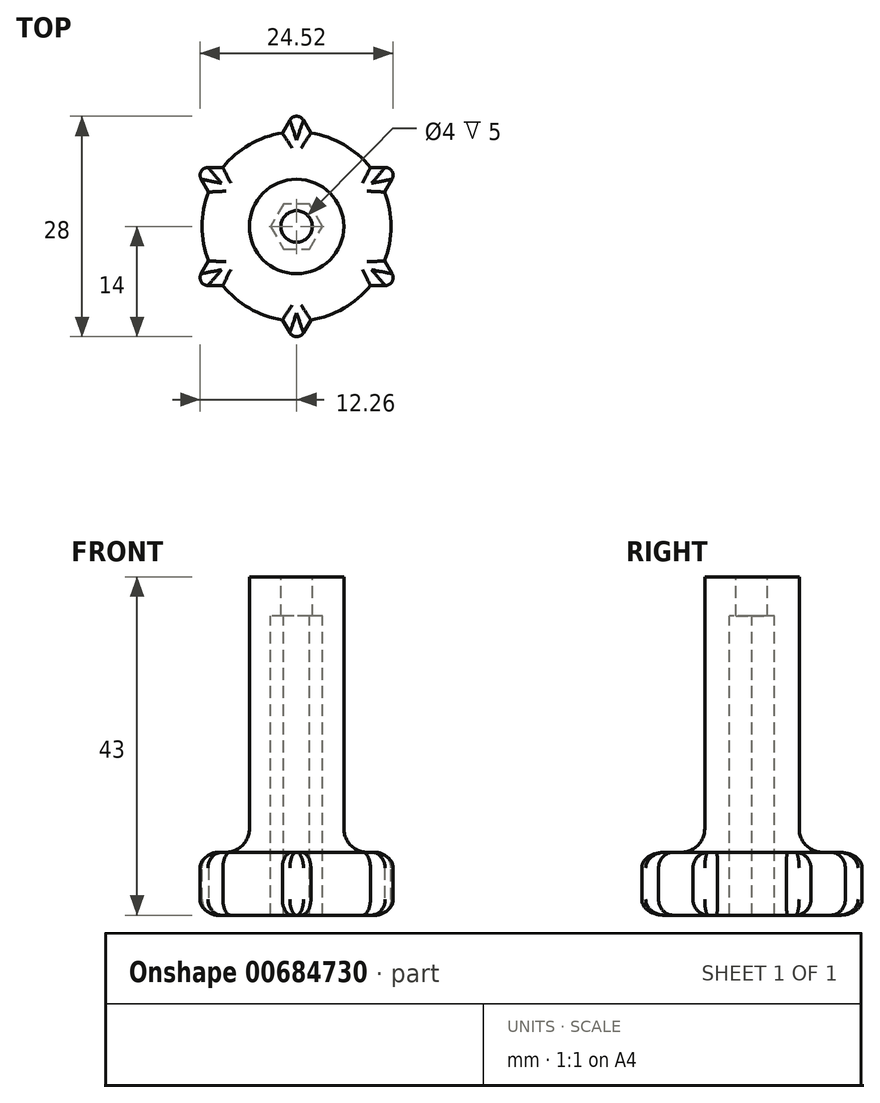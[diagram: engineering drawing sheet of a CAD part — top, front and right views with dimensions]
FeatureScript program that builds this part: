
annotation { "Feature Type Name" : "Feature", "Feature Type Description" : "" }
export const myFeature = defineFeature(function(context is Context, id is Id, definition is map)
    precondition{}
    {
        {
            var Q0;
            Q0=qCreatedBy(makeId("Front.planeOp"),FACE);
            var sketch = newSketch(context, id + "F0", { "sketchPlane" : qUnion([Q0])});
            skLineSegment(sketch, "E0", {"start": v(0, 0) * mm, "end": v(12, 0) * mm});
            skLineSegment(sketch, "E1", {"start": v(12, 0) * mm, "end": v(12, 8) * mm});
            skLineSegment(sketch, "E2", {"start": v(12, 8) * mm, "end": v(6, 8) * mm});
            skLineSegment(sketch, "E3", {"start": v(6, 8) * mm, "end": v(6, 43) * mm});
            skLineSegment(sketch, "E4", {"start": v(6, 43) * mm, "end": v(0, 43) * mm});
            skLineSegment(sketch, "E5", {"start": v(0, 43) * mm, "end": v(0, 0) * mm});
            skSolve(sketch);
        }
        {
            var Q0;
            Q0=makeQuery(id+"F0.imprint","IMPRINT",FACE,{"disambiguationData":[TD([[makeQuery(id+"F0.imprint","IMPRINT",EDGE,{"derivedFrom":sQuery(id+"F0.wireOp",EDGE,"E0")}),1.0]])]});
            var Q1;
            Q1=sQuery(id+"F0.wireOp",EDGE,"E5");
            revolve(context, id + "F1", {"surfaceOperationType" : NewSurfaceOperationType.NEW, "entities" : qUnion([Q0]), "axis" : qUnion([Q1]), "revolveType" : RevolveType.FULL});
        }
        {
            var Q0;
            Q0=makeQuery(id+"F1.opRevolve","SWEPT_EDGE",EDGE,{"disambiguationData":[OSD([sQuery(id+"F0.wireOp",EDGE,"E2"),sQuery(id+"F0.wireOp",EDGE,"E3")])]});
            fillet(context, id + "F2", {"entities" : qUnion([Q0]), "radius" : 3 * mm, "tangentPropagation" : true, "allowEdgeOverflow" : false});
        }
        {
            var Q0;
            Q0=makeQuery(id+"F1.opRevolve","SWEPT_FACE",FACE,{"disambiguationData":[OSD([sQuery(id+"F0.wireOp",EDGE,"E4")])]});
            var sketch = newSketch(context, id + "F3", { "sketchPlane" : qUnion([Q0])});
            skCircle(sketch, "E6", {"center": v(0, 0) * mm, "radius": 2 * mm});
            skCircle(sketch, "E7.cCircle", {"center": v(0, 0) * mm, "radius": 2.85 * mm, "construction": true});
            skLineSegment(sketch, "E7.0", {"start": v(1.65, 2.85) * mm, "end": v(3.3, 0) * mm});
            skLineSegment(sketch, "E7.1", {"start": v(3.3, 0) * mm, "end": v(1.65, -2.85) * mm});
            skLineSegment(sketch, "E7.2", {"start": v(1.65, -2.85) * mm, "end": v(-1.65, -2.85) * mm});
            skLineSegment(sketch, "E7.3", {"start": v(-1.65, -2.85) * mm, "end": v(-3.3, 0) * mm});
            skLineSegment(sketch, "E7.4", {"start": v(-3.3, 0) * mm, "end": v(-1.65, 2.85) * mm});
            skLineSegment(sketch, "E7.5", {"start": v(-1.65, 2.85) * mm, "end": v(1.65, 2.85) * mm});
            skPoint(sketch, "E7.0.midPoint", {"position": v(2.47, 1.43) * mm});
            skSolve(sketch);
        }
        {
            var Q0;
            Q0=makeQuery(id+"F1.opRevolve","SWEPT_FACE",FACE,{"disambiguationData":[OSD([sQuery(id+"F0.wireOp",EDGE,"E0")])]});
            var sketch = newSketch(context, id + "F4", { "sketchPlane" : qUnion([Q0])});
            skLineSegment(sketch, "E8", {"start": v(0, 0) * mm, "end": v(0, -15) * mm, "construction": true});
            skLineSegment(sketch, "E9", {"start": v(-0.87, -13.5) * mm, "end": v(-1.81, -11.86) * mm});
            skLineSegment(sketch, "E10.MirrorCS", {"start": v(0.87, -13.5) * mm, "end": v(1.81, -11.86) * mm});
            skLineSegment(sketch, "E11", {"start": v(-1.81, -11.86) * mm, "end": v(1.81, -11.86) * mm});
            skPoint(sketch, "E12.visualSharp", {"position": v(0, -15) * mm});
            skArc(sketch, "E12.filletArc", {"start": v(-0.87, -13.5) * mm, "mid": v(0, -14) * mm, "end": v(0.87, -13.5) * mm});
            skArc(sketch, "E13.1.0", {"start": v(-12.12, -6) * mm, "mid": v(-12.12, -7) * mm, "end": v(-11.26, -7.5) * mm});
            skLineSegment(sketch, "E13.1.1", {"start": v(-11.26, -7.5) * mm, "end": v(-9.37, -7.5) * mm});
            skLineSegment(sketch, "E13.1.2", {"start": v(-12.12, -6) * mm, "end": v(-11.18, -4.36) * mm});
            skLineSegment(sketch, "E13.1.3", {"start": v(-11.18, -4.36) * mm, "end": v(-9.37, -7.5) * mm});
            skArc(sketch, "E13.2.0", {"start": v(-11.26, 7.5) * mm, "mid": v(-12.12, 7) * mm, "end": v(-12.12, 6) * mm});
            skLineSegment(sketch, "E13.2.1", {"start": v(-12.12, 6) * mm, "end": v(-11.18, 4.36) * mm});
            skLineSegment(sketch, "E13.2.2", {"start": v(-11.26, 7.5) * mm, "end": v(-9.37, 7.5) * mm});
            skLineSegment(sketch, "E13.2.3", {"start": v(-9.37, 7.5) * mm, "end": v(-11.18, 4.36) * mm});
            skArc(sketch, "E13.3.0", {"start": v(0.87, 13.5) * mm, "mid": v(0, 14) * mm, "end": v(-0.87, 13.5) * mm});
            skLineSegment(sketch, "E13.3.1", {"start": v(-0.87, 13.5) * mm, "end": v(-1.81, 11.86) * mm});
            skLineSegment(sketch, "E13.3.2", {"start": v(0.87, 13.5) * mm, "end": v(1.81, 11.86) * mm});
            skLineSegment(sketch, "E13.3.3", {"start": v(1.81, 11.86) * mm, "end": v(-1.81, 11.86) * mm});
            skArc(sketch, "E13.4.0", {"start": v(12.12, 6) * mm, "mid": v(12.12, 7) * mm, "end": v(11.26, 7.5) * mm});
            skLineSegment(sketch, "E13.4.1", {"start": v(11.26, 7.5) * mm, "end": v(9.37, 7.5) * mm});
            skLineSegment(sketch, "E13.4.2", {"start": v(12.12, 6) * mm, "end": v(11.18, 4.36) * mm});
            skLineSegment(sketch, "E13.4.3", {"start": v(11.18, 4.36) * mm, "end": v(9.37, 7.5) * mm});
            skArc(sketch, "E13.5.0", {"start": v(11.26, -7.5) * mm, "mid": v(12.12, -7) * mm, "end": v(12.12, -6) * mm});
            skLineSegment(sketch, "E13.5.1", {"start": v(12.12, -6) * mm, "end": v(11.18, -4.36) * mm});
            skLineSegment(sketch, "E13.5.2", {"start": v(11.26, -7.5) * mm, "end": v(9.37, -7.5) * mm});
            skLineSegment(sketch, "E13.5.3", {"start": v(9.37, -7.5) * mm, "end": v(11.18, -4.36) * mm});
            skPoint(sketch, "E13.center", {"position": v(0, 0) * mm});
            skLineSegment(sketch, "E13.anchor1", {"start": v(0, 0) * mm, "end": v(-0.87, -13.5) * mm, "construction": true});
            skLineSegment(sketch, "E13.anchor2", {"start": v(0, 0) * mm, "end": v(11.26, -7.5) * mm, "construction": true});
            skSolve(sketch);
        }
        {
            var Q0;
            Q0 = qSketchRegion(id + "F4", true);
            var Q1;
            Q1=makeQuery(id+"F1.opRevolve","SWEPT_FACE",FACE,{"disambiguationData":[OSD([sQuery(id+"F0.wireOp",EDGE,"E2")])]});
            extrude(context, id + "F5", {"entities" : qUnion([Q0]), "operationType" : NewBodyOperationType.ADD, "endBound" : BoundingType.UP_TO_SURFACE, "oppositeDirection" : true, "depth" : 25 * mm, "endBoundEntityFace" : qUnion([Q1]), "offsetDistance" : 25 * mm});
        }
        {
            var Q0;
            {var subQ0=sQuery(id+"F0.wireOp",EDGE,"E2");Q0=makeQuery(id+"F5.boolean.opBoolean","MERGE",FACE,{"derivedFrom":[makeQuery(id+"F1.opRevolve","SWEPT_FACE",FACE,{"disambiguationData":[OSD([subQ0])]}),makeQuery(id+"F5.opExtrude","CAP_FACE",FACE,{"disambiguationData":[OSD([subQ0]),OD(0.0)],"isStart":false}),makeQuery(id+"F5.opExtrude","CAP_FACE",FACE,{"disambiguationData":[OSD([subQ0]),OD(1.0)],"isStart":false}),makeQuery(id+"F5.opExtrude","CAP_FACE",FACE,{"disambiguationData":[OSD([subQ0]),OD(2.0)],"isStart":false}),makeQuery(id+"F5.opExtrude","CAP_FACE",FACE,{"disambiguationData":[OSD([subQ0]),OD(3.0)],"isStart":false}),makeQuery(id+"F5.opExtrude","CAP_FACE",FACE,{"disambiguationData":[OSD([subQ0]),OD(4.0)],"isStart":false}),makeQuery(id+"F5.opExtrude","CAP_FACE",FACE,{"disambiguationData":[OSD([subQ0]),OD(5.0)],"isStart":false})]});}
            var Q1;
            Q1=makeQuery(id+"F5.boolean.opBoolean","MERGE",FACE,{"derivedFrom":[makeQuery(id+"F1.opRevolve","SWEPT_FACE",FACE,{"disambiguationData":[OSD([sQuery(id+"F0.wireOp",EDGE,"E0")])]}),makeQuery(id+"F5.opExtrude","CAP_FACE",FACE,{"disambiguationData":[OSD([sQuery(id+"F4.wireOp",EDGE,"E9"),sQuery(id+"F4.wireOp",EDGE,"E10.MirrorCS"),sQuery(id+"F4.wireOp",EDGE,"E11"),sQuery(id+"F4.wireOp",EDGE,"E12.filletArc")])],"isStart":true}),makeQuery(id+"F5.opExtrude","CAP_FACE",FACE,{"disambiguationData":[OSD([sQuery(id+"F4.wireOp",EDGE,"E13.1.0"),sQuery(id+"F4.wireOp",EDGE,"E13.1.1"),sQuery(id+"F4.wireOp",EDGE,"E13.1.2"),sQuery(id+"F4.wireOp",EDGE,"E13.1.3")])],"isStart":true}),makeQuery(id+"F5.opExtrude","CAP_FACE",FACE,{"disambiguationData":[OSD([sQuery(id+"F4.wireOp",EDGE,"E13.2.0"),sQuery(id+"F4.wireOp",EDGE,"E13.2.1"),sQuery(id+"F4.wireOp",EDGE,"E13.2.2"),sQuery(id+"F4.wireOp",EDGE,"E13.2.3")])],"isStart":true}),makeQuery(id+"F5.opExtrude","CAP_FACE",FACE,{"disambiguationData":[OSD([sQuery(id+"F4.wireOp",EDGE,"E13.3.0"),sQuery(id+"F4.wireOp",EDGE,"E13.3.1"),sQuery(id+"F4.wireOp",EDGE,"E13.3.2"),sQuery(id+"F4.wireOp",EDGE,"E13.3.3")])],"isStart":true}),makeQuery(id+"F5.opExtrude","CAP_FACE",FACE,{"disambiguationData":[OSD([sQuery(id+"F4.wireOp",EDGE,"E13.4.0"),sQuery(id+"F4.wireOp",EDGE,"E13.4.1"),sQuery(id+"F4.wireOp",EDGE,"E13.4.2"),sQuery(id+"F4.wireOp",EDGE,"E13.4.3")])],"isStart":true}),makeQuery(id+"F5.opExtrude","CAP_FACE",FACE,{"disambiguationData":[OSD([sQuery(id+"F4.wireOp",EDGE,"E13.5.0"),sQuery(id+"F4.wireOp",EDGE,"E13.5.1"),sQuery(id+"F4.wireOp",EDGE,"E13.5.2"),sQuery(id+"F4.wireOp",EDGE,"E13.5.3")])],"isStart":true})]});
            fillet(context, id + "F6", {"entities" : qUnion([Q0, Q1]), "radius" : 2 * mm, "tangentPropagation" : true, "allowEdgeOverflow" : false});
        }
        {
            var Q0;
            Q0=makeQuery(id+"F3.imprint","IMPRINT",FACE,{"disambiguationData":[TD([[makeQuery(id+"F3.imprint","IMPRINT",EDGE,{"derivedFrom":sQuery(id+"F3.wireOp",EDGE,"E6")}),-1.0]])]});
            var Q1;
            Q1=makeQuery(id+"F3.imprint","IMPRINT",FACE,{"disambiguationData":[TD([[makeQuery(id+"F3.imprint","IMPRINT",EDGE,{"derivedFrom":sQuery(id+"F3.wireOp",EDGE,"E6")}),1.0]])]});
            var Q2;
            Q2=makeQuery(id+"F5.boolean.opBoolean","MERGE",FACE,{"derivedFrom":[makeQuery(id+"F1.opRevolve","SWEPT_FACE",FACE,{"disambiguationData":[OSD([sQuery(id+"F0.wireOp",EDGE,"E0")])]}),makeQuery(id+"F5.opExtrude","CAP_FACE",FACE,{"disambiguationData":[OSD([sQuery(id+"F4.wireOp",EDGE,"E9"),sQuery(id+"F4.wireOp",EDGE,"E10.MirrorCS"),sQuery(id+"F4.wireOp",EDGE,"E11"),sQuery(id+"F4.wireOp",EDGE,"E12.filletArc")])],"isStart":true}),makeQuery(id+"F5.opExtrude","CAP_FACE",FACE,{"disambiguationData":[OSD([sQuery(id+"F4.wireOp",EDGE,"E13.1.0"),sQuery(id+"F4.wireOp",EDGE,"E13.1.1"),sQuery(id+"F4.wireOp",EDGE,"E13.1.2"),sQuery(id+"F4.wireOp",EDGE,"E13.1.3")])],"isStart":true}),makeQuery(id+"F5.opExtrude","CAP_FACE",FACE,{"disambiguationData":[OSD([sQuery(id+"F4.wireOp",EDGE,"E13.2.0"),sQuery(id+"F4.wireOp",EDGE,"E13.2.1"),sQuery(id+"F4.wireOp",EDGE,"E13.2.2"),sQuery(id+"F4.wireOp",EDGE,"E13.2.3")])],"isStart":true}),makeQuery(id+"F5.opExtrude","CAP_FACE",FACE,{"disambiguationData":[OSD([sQuery(id+"F4.wireOp",EDGE,"E13.3.0"),sQuery(id+"F4.wireOp",EDGE,"E13.3.1"),sQuery(id+"F4.wireOp",EDGE,"E13.3.2"),sQuery(id+"F4.wireOp",EDGE,"E13.3.3")])],"isStart":true}),makeQuery(id+"F5.opExtrude","CAP_FACE",FACE,{"disambiguationData":[OSD([sQuery(id+"F4.wireOp",EDGE,"E13.4.0"),sQuery(id+"F4.wireOp",EDGE,"E13.4.1"),sQuery(id+"F4.wireOp",EDGE,"E13.4.2"),sQuery(id+"F4.wireOp",EDGE,"E13.4.3")])],"isStart":true}),makeQuery(id+"F5.opExtrude","CAP_FACE",FACE,{"disambiguationData":[OSD([sQuery(id+"F4.wireOp",EDGE,"E13.5.0"),sQuery(id+"F4.wireOp",EDGE,"E13.5.1"),sQuery(id+"F4.wireOp",EDGE,"E13.5.2"),sQuery(id+"F4.wireOp",EDGE,"E13.5.3")])],"isStart":true})]});
            extrude(context, id + "F7", {"entities" : qUnion([Q0, Q1]), "operationType" : NewBodyOperationType.REMOVE, "endBound" : BoundingType.UP_TO_SURFACE, "oppositeDirection" : true, "depth" : 25 * mm, "endBoundEntityFace" : qUnion([Q2]), "offsetDistance" : 25 * mm, "hasSecondDirection" : true, "secondDirectionOppositeDirection" : true, "secondDirectionDepth" : 5 * mm});
        }
        {
            var Q0;
            Q0=makeQuery(id+"F3.imprint","IMPRINT",FACE,{"disambiguationData":[TD([[makeQuery(id+"F3.imprint","IMPRINT",EDGE,{"derivedFrom":sQuery(id+"F3.wireOp",EDGE,"E6")}),1.0]])]});
            extrude(context, id + "F8", {"entities" : qUnion([Q0]), "operationType" : NewBodyOperationType.REMOVE, "oppositeDirection" : true, "depth" : 25 * mm, "offsetDistance" : 25 * mm});
        }
    });
